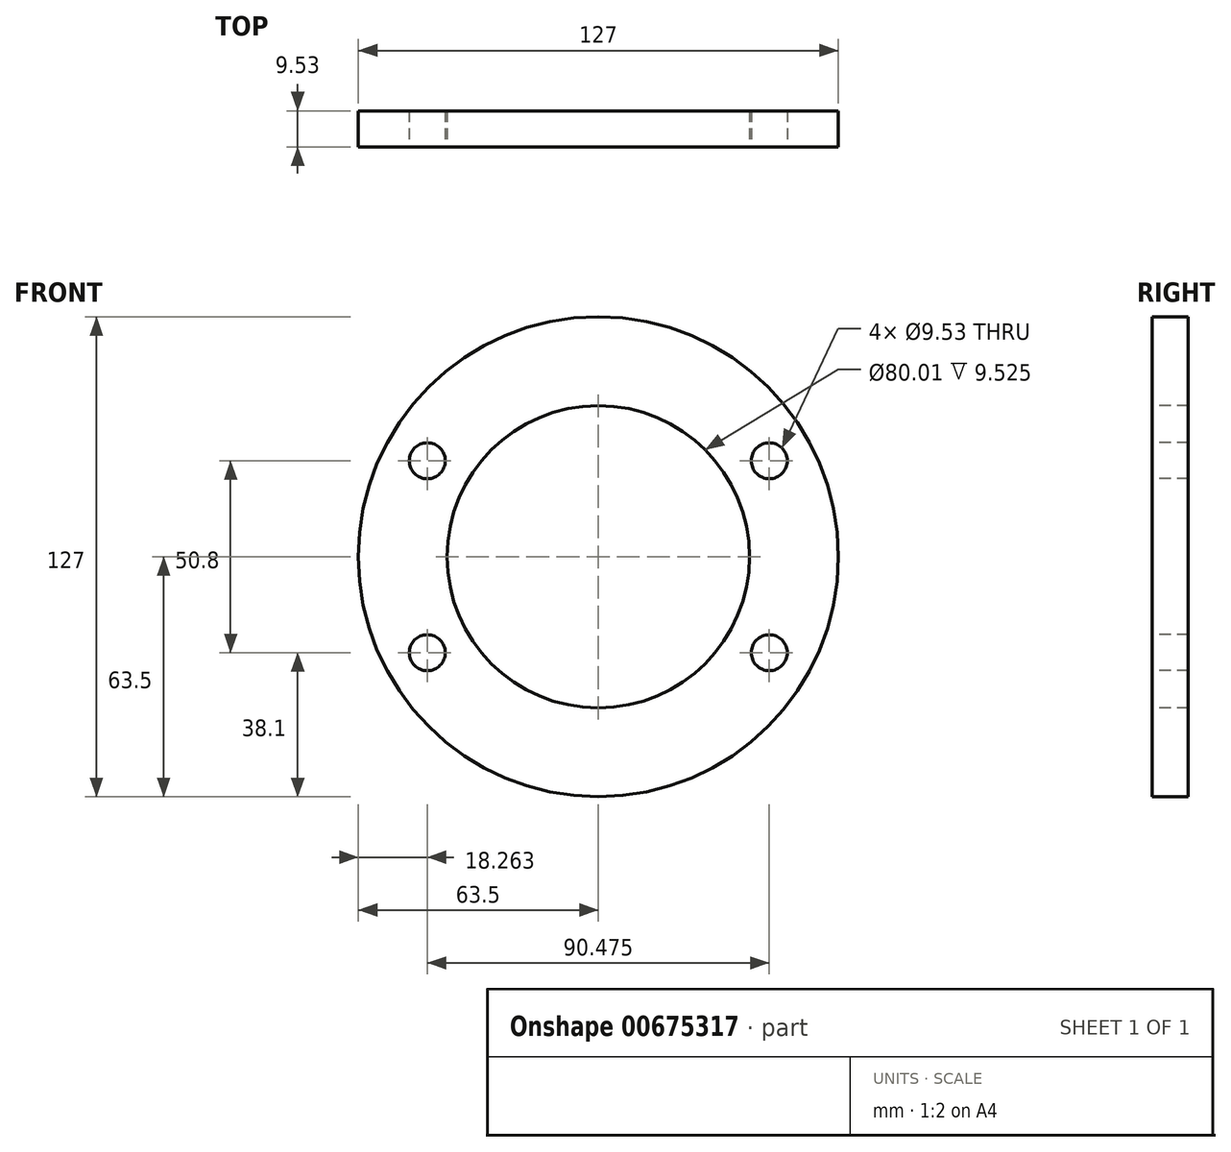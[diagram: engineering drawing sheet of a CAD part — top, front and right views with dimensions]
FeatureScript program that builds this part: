
annotation { "Feature Type Name" : "Feature", "Feature Type Description" : "" }
export const myFeature = defineFeature(function(context is Context, id is Id, definition is map)
    precondition{}
    {
        {
            var Q0;
            Q0=qCreatedBy(makeId("Front.planeOp"),FACE);
            var sketch = newSketch(context, id + "F0", { "sketchPlane" : qUnion([Q0])});
            skCircle(sketch, "E0", {"center": v(0, 0) * mm, "radius": 40 * mm});
            skCircle(sketch, "E1", {"center": v(45.24, 25.4) * mm, "radius": 4.76 * mm});
            skCircle(sketch, "E2.MirrorC", {"center": v(45.24, -25.4) * mm, "radius": 4.76 * mm});
            skCircle(sketch, "E3.MirrorC", {"center": v(-45.24, 25.4) * mm, "radius": 4.76 * mm});
            skCircle(sketch, "E4.MirrorC", {"center": v(-45.24, -25.4) * mm, "radius": 4.76 * mm});
            skCircle(sketch, "E5", {"center": v(0, 0) * mm, "radius": 63.5 * mm});
            skSolve(sketch);
        }
        {
            var Q0;
            Q0 = qSketchRegion(id + "F0", true);
            extrude(context, id + "F1", {"entities" : qUnion([Q0]), "oppositeDirection" : true, "depth" : 9.52 * mm, "offsetDistance" : 25.4 * mm});
        }
    });
